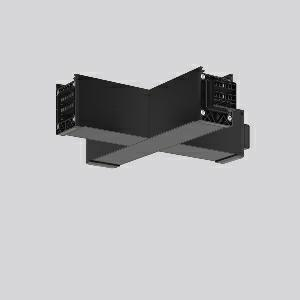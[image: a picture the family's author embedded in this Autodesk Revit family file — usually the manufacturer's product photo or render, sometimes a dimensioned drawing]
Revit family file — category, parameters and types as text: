
# Revit family: linedo_x-verbindung_982775_003_1_6943
name_source: partatom
category: Lighting Fixtures
units: mm (PartAtom-declared; Revit-internal decimal feet)

## family parameters
Cut with Voids When Loaded = No
Host = Face
Light Source = No
Part Type = Normal
Room Calculation Point = No
Round Connector Dimension = Use Diameter
Shared = No

## types (1)
- LINEDO X-Verbindung
    Apparent Load = 0 VA
    Default Elevation = 1800 mm
    Description = Series: LINEDO
X-connector, 7-pole, connection plug / socket / plug / socket. Housing: extruded aluminium profile, powder-coated. Cover made of plastic, surface like housing. LINEDO plug system, plastic, black. Easy connection for rigid or flexible wires. 6 membrane cable entries (2 x M20 and 4 x M25). Suitable for power supply in 7-pole version. Ready prewired. Colour-coded individual cables enable easy electromechanical separation.
Colour: jet black (RAL 9005)
Length: 330 mm
Width: 330 mm
Height: 76 mm
Weight: 1230 g
    Height = 76 mm
    Lamp = 0 x
    Length = 331 mm
    Luminous efficacy = 0 lm/W
    Manufacturer = RZB
    ModVariant = No
    Model = 982775.003.1
    Mounting Place = Ceiling
    Mounting Type = Surface mounted
    Number of Poles = 1
    OnlyDefault = Yes
    Power Factor = 1
    Product Name = LINEDO X-Verbindung
    Product group = Surface mounted continuous line luminaire system
    ProductGroupID = 310
    Protection Class = Protection class I
    Protection Degree = Degree of protection
    RLX_Detail_Level = 1
    RLX_Emergency_Light_Flux = 0 lm
    RLX_Emergency_Type = 0
    RLX_Emergency_Type_DB = No
    RlxData = <blob elided: 22757 chars, md5=f46cb262>
    Standby Power = 0 W
    System Light Flux = 0 lm
    System Power = 0 W
    Type Comments = Product without accessories
    Type Image = 982775.003.jpg
    URL = http://relux.com
    VarID = ---
    Voltage = 0 V
    Weight = 0.00 kg
    Width = 331 mm

## geometry (parser evidence)
native form markers: Blend x4, Sweep x11
no freeform markers — native parametric forms only
